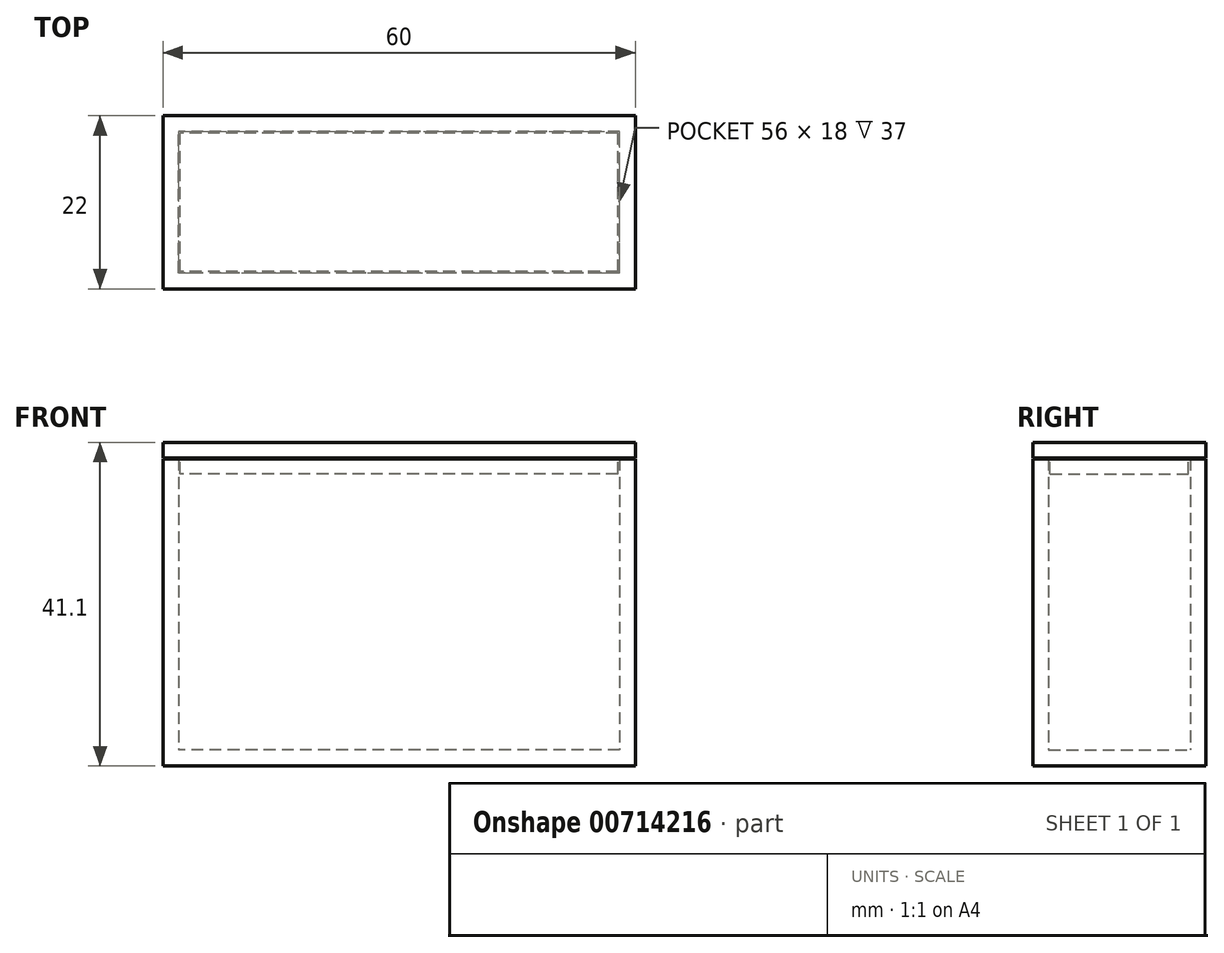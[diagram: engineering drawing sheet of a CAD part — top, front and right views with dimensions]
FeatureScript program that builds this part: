
annotation { "Feature Type Name" : "Feature", "Feature Type Description" : "" }
export const myFeature = defineFeature(function(context is Context, id is Id, definition is map)
    precondition{}
    {
        {
            var Q0;
            Q0=qCreatedBy(makeId("Top.planeOp"),FACE);
            var sketch = newSketch(context, id + "F0", { "sketchPlane" : qUnion([Q0])});
            skLineSegment(sketch, "E0.bottom", {"start": v(30, -11) * mm, "end": v(-30, -11) * mm});
            skLineSegment(sketch, "E0.top", {"start": v(30, 11) * mm, "end": v(-30, 11) * mm});
            skLineSegment(sketch, "E0.left", {"start": v(30, -11) * mm, "end": v(30, 11) * mm});
            skLineSegment(sketch, "E0.right", {"start": v(-30, -11) * mm, "end": v(-30, 11) * mm});
            skPoint(sketch, "E0.middle", {"position": v(0, 0) * mm});
            skSolve(sketch);
        }
        {
            var Q0;
            Q0=makeQuery(id+"F0.imprint","IMPRINT",FACE,{"disambiguationData":[TD([[makeQuery(id+"F0.imprint","IMPRINT",EDGE,{"derivedFrom":sQuery(id+"F0.wireOp",EDGE,"E0.bottom")}),-1.0]])]});
            extrude(context, id + "F1", {"entities" : qUnion([Q0]), "depth" : 39 * mm, "offsetDistance" : 25 * mm});
        }
        {
            var Q0;
            Q0=makeQuery(id+"F1.opExtrude","CAP_FACE",FACE,{"disambiguationData":[OSD([sQuery(id+"F0.wireOp",EDGE,"E0.bottom"),sQuery(id+"F0.wireOp",EDGE,"E0.top"),sQuery(id+"F0.wireOp",EDGE,"E0.left"),sQuery(id+"F0.wireOp",EDGE,"E0.right")])],"isStart":false});
            shell(context, id + "F2", {"entities" : qUnion([Q0]), "thickness" : 2 * mm});
        }
        {
            var Q0;
            Q0=makeQuery(id+"F1.opExtrude","CAP_FACE",FACE,{"disambiguationData":[OSD([sQuery(id+"F0.wireOp",EDGE,"E0.bottom"),sQuery(id+"F0.wireOp",EDGE,"E0.top"),sQuery(id+"F0.wireOp",EDGE,"E0.left"),sQuery(id+"F0.wireOp",EDGE,"E0.right")])],"isStart":false});
            cPlane(context, id + "F3", {"entities" : qUnion([Q0]), "cplaneType" : CPlaneType.OFFSET, "offset" : .1 * mm, "width" : 150 * mm, "height" : 150 * mm});
        }
        {
            var Q0;
            Q0=qCreatedBy(id+"F3.planeOp",FACE);
            var sketch = newSketch(context, id + "F4", { "sketchPlane" : qUnion([Q0])});
            skLineSegment(sketch, "E1.0.0", {"start": v(30, -11) * mm, "end": v(30, 11) * mm});
            skLineSegment(sketch, "E1.0.1", {"start": v(30, 11) * mm, "end": v(-30, 11) * mm});
            skLineSegment(sketch, "E1.0.2", {"start": v(-30, 11) * mm, "end": v(-30, -11) * mm});
            skLineSegment(sketch, "E1.0.3", {"start": v(-30, -11) * mm, "end": v(30, -11) * mm});
            skLineSegment(sketch, "E2.0", {"start": v(28, -9) * mm, "end": v(-28, -9) * mm});
            skLineSegment(sketch, "E2.1", {"start": v(-28, -9) * mm, "end": v(-28, 9) * mm});
            skLineSegment(sketch, "E2.2", {"start": v(28, 9) * mm, "end": v(-28, 9) * mm});
            skLineSegment(sketch, "E2.3", {"start": v(28, -9) * mm, "end": v(28, 9) * mm});
            skLineSegment(sketch, "E3.0", {"start": v(27.8, -8.8) * mm, "end": v(-27.8, -8.8) * mm});
            skLineSegment(sketch, "E3.1", {"start": v(27.8, -8.8) * mm, "end": v(27.8, 8.8) * mm});
            skLineSegment(sketch, "E3.2", {"start": v(27.8, 8.8) * mm, "end": v(-27.8, 8.8) * mm});
            skLineSegment(sketch, "E3.3", {"start": v(-27.8, -8.8) * mm, "end": v(-27.8, 8.8) * mm});
            skSolve(sketch);
        }
        {
            var Q0;
            Q0 = qSketchRegion(id + "F4", true);
            var Q1;
            Q1=makeQuery(id+"F4.imprint","IMPRINT",FACE,{"disambiguationData":[TD([[makeQuery(id+"F4.imprint","IMPRINT",EDGE,{"derivedFrom":sQuery(id+"F4.wireOp",EDGE,"E2.0")}),-1.0]])]});
            var Q2;
            Q2=makeQuery(id+"F4.imprint","IMPRINT",FACE,{"disambiguationData":[TD([[makeQuery(id+"F4.imprint","IMPRINT",EDGE,{"derivedFrom":sQuery(id+"F4.wireOp",EDGE,"E3.0")}),-1.0]])]});
            extrude(context, id + "F5", {"entities" : qUnion([Q0, Q1, Q2]), "depth" : 2 * mm, "offsetDistance" : 25 * mm});
        }
        {
            var Q0;
            Q0=makeQuery(id+"F4.imprint","IMPRINT",FACE,{"disambiguationData":[TD([[makeQuery(id+"F4.imprint","IMPRINT",EDGE,{"derivedFrom":sQuery(id+"F4.wireOp",EDGE,"E3.0")}),-1.0]])]});
            extrude(context, id + "F6", {"entities" : qUnion([Q0]), "operationType" : NewBodyOperationType.ADD, "oppositeDirection" : true, "depth" : 2 * mm, "offsetDistance" : 25 * mm});
        }
    });
